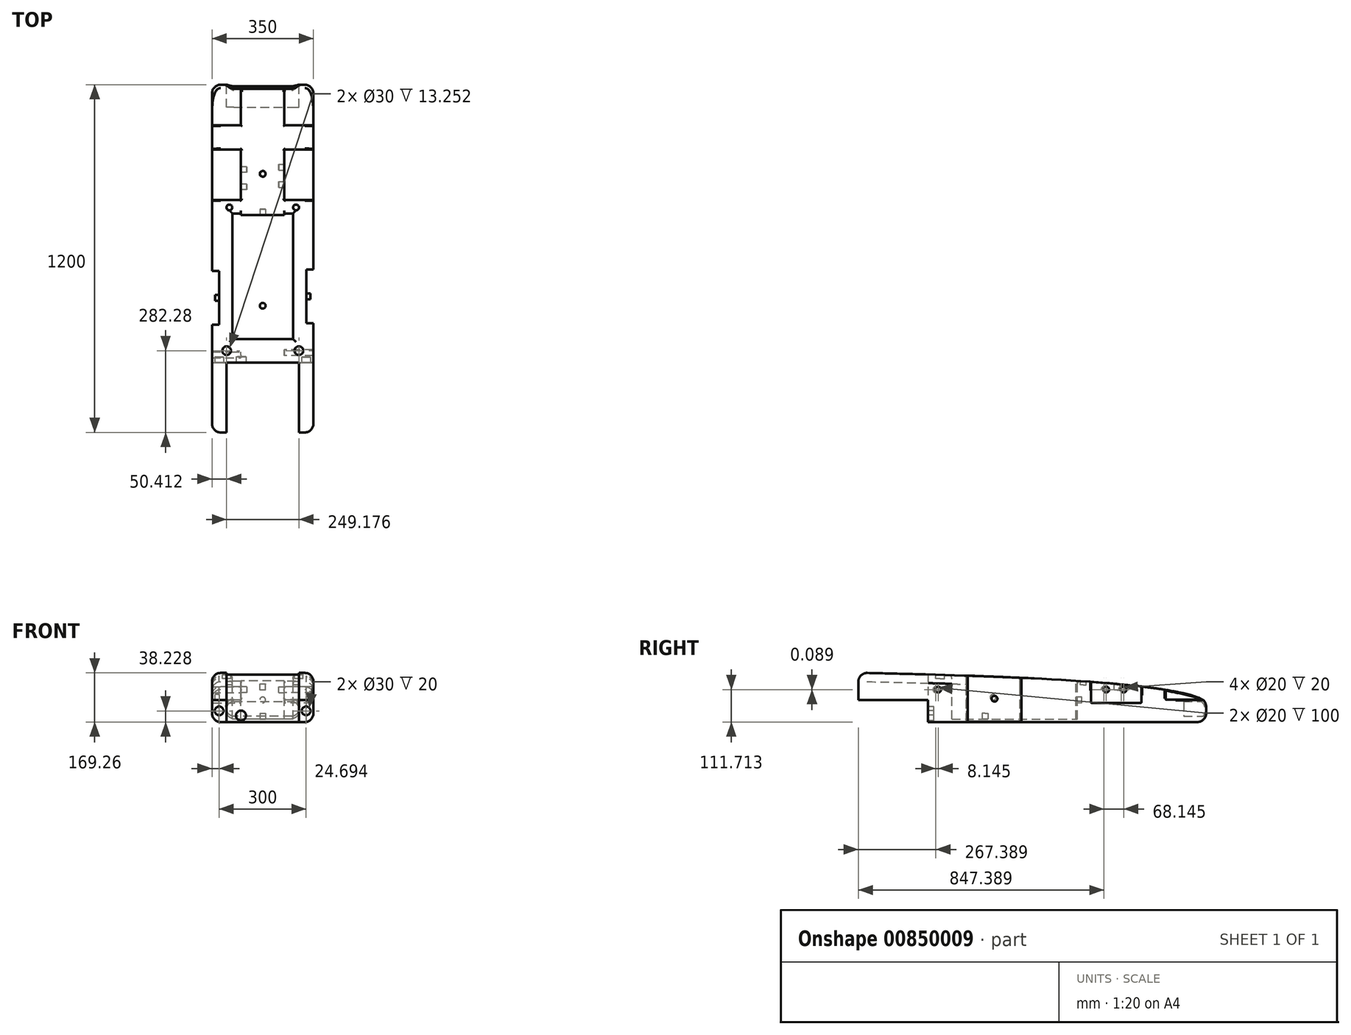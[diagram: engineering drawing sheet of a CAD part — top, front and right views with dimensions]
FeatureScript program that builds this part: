
annotation { "Feature Type Name" : "Feature", "Feature Type Description" : "" }
export const myFeature = defineFeature(function(context is Context, id is Id, definition is map)
    precondition{}
    {
        {
            var Q0;
            Q0=qCreatedBy(makeId("Right.planeOp"),FACE);
            var sketch = newSketch(context, id + "F0", { "sketchPlane" : qUnion([Q0])});
            skLineSegment(sketch, "E0", {"start": v(-322.28, 0) * mm, "end": v(877.72, 0) * mm});
            skLineSegment(sketch, "E1", {"start": v(-322.28, 0) * mm, "end": v(-322.28, 170) * mm});
            skLineSegment(sketch, "E2", {"start": v(877.72, 0) * mm, "end": v(877.72, 70) * mm});
            skFitSpline(sketch, "E3", {"points": [v(877.72, 70) * mm, v(-322.28, 170) * mm], "startDerivative": vector(-305.27, 234.76) * mm, "endDerivative": vector(-966.84, 23.9) * mm});
            skSolve(sketch);
        }
        {
            var Q0;
            Q0=makeQuery(id+"F0.imprint","IMPRINT",FACE,{"disambiguationData":[TD([[makeQuery(id+"F0.imprint","IMPRINT",EDGE,{"derivedFrom":sQuery(id+"F0.wireOp",EDGE,"E0")}),1.0]])]});
            extrude(context, id + "F1", {"entities" : qUnion([Q0]), "endBound" : BoundingType.SYMMETRIC, "depth" : 350 * mm, "offsetDistance" : 25 * mm});
        }
        {
            var Q0;
            Q0=makeQuery(id+"F1.opExtrude","SWEPT_EDGE",EDGE,{"disambiguationData":[OSD([sQuery(id+"F0.wireOp",EDGE,"E2"),sQuery(id+"F0.wireOp",EDGE,"E3")])]});
            var Q1;
            Q1=makeQuery(id+"F1.opExtrude","CAP_EDGE",EDGE,{"disambiguationData":[OSD([sQuery(id+"F0.wireOp",EDGE,"E2")])],"isStart":false});
            var Q2;
            Q2=makeQuery(id+"F1.opExtrude","SWEPT_EDGE",EDGE,{"disambiguationData":[OSD([sQuery(id+"F0.wireOp",EDGE,"E0"),sQuery(id+"F0.wireOp",EDGE,"E2")])]});
            var Q3;
            Q3=makeQuery(id+"F1.opExtrude","CAP_EDGE",EDGE,{"disambiguationData":[OSD([sQuery(id+"F0.wireOp",EDGE,"E2")])],"isStart":true});
            var Q4;
            Q4=makeQuery(id+"F1.opExtrude","CAP_EDGE",EDGE,{"disambiguationData":[OSD([sQuery(id+"F0.wireOp",EDGE,"E0")])],"isStart":false});
            var Q5;
            Q5=makeQuery(id+"F1.opExtrude","CAP_EDGE",EDGE,{"disambiguationData":[OSD([sQuery(id+"F0.wireOp",EDGE,"E3")])],"isStart":false});
            var Q6;
            Q6=makeQuery(id+"F1.opExtrude","CAP_EDGE",EDGE,{"disambiguationData":[OSD([sQuery(id+"F0.wireOp",EDGE,"E1")])],"isStart":false});
            var Q7;
            Q7=makeQuery(id+"F1.opExtrude","CAP_EDGE",EDGE,{"disambiguationData":[OSD([sQuery(id+"F0.wireOp",EDGE,"E0")])],"isStart":true});
            var Q8;
            Q8=makeQuery(id+"F1.opExtrude","CAP_EDGE",EDGE,{"disambiguationData":[OSD([sQuery(id+"F0.wireOp",EDGE,"E3")])],"isStart":true});
            var Q9;
            Q9=makeQuery(id+"F1.opExtrude","CAP_EDGE",EDGE,{"disambiguationData":[OSD([sQuery(id+"F0.wireOp",EDGE,"E1")])],"isStart":true});
            var Q10;
            Q10=makeQuery(id+"F1.opExtrude","SWEPT_EDGE",EDGE,{"disambiguationData":[OSD([sQuery(id+"F0.wireOp",EDGE,"E1"),sQuery(id+"F0.wireOp",EDGE,"E3")])]});
            var Q11;
            Q11=makeQuery(id+"F1.opExtrude","SWEPT_EDGE",EDGE,{"disambiguationData":[OSD([sQuery(id+"F0.wireOp",EDGE,"E0"),sQuery(id+"F0.wireOp",EDGE,"E1")])]});
            fillet(context, id + "F2", {"entities" : qUnion([Q0, Q1, Q2, Q3, Q4, Q5, Q6, Q7, Q8, Q9, Q10, Q11]), "radius" : 30 * mm, "tangentPropagation" : true, "allowEdgeOverflow" : false});
        }
        {
            var Q0;
            Q0=qCreatedBy(makeId("Front.planeOp"),FACE);
            cPlane(context, id + "F3", {"entities" : qUnion([Q0]), "cplaneType" : CPlaneType.OFFSET, "offset" : 1500 * mm, "oppositeDirection" : true, "width" : 150 * mm, "height" : 150 * mm});
        }
        {
            var Q0;
            Q0=qCreatedBy(id+"F3.planeOp",FACE);
            var sketch = newSketch(context, id + "F4", { "sketchPlane" : qUnion([Q0])});
            skLineSegment(sketch, "E4.bottom", {"start": v(-100, 20.2) * mm, "end": v(100, 20.2) * mm});
            skLineSegment(sketch, "E4.top", {"start": v(-100, 70.2) * mm, "end": v(100, 70.2) * mm});
            skLineSegment(sketch, "E4.left", {"start": v(-100, 20.2) * mm, "end": v(-100, 70.2) * mm});
            skLineSegment(sketch, "E4.right", {"start": v(100, 20.2) * mm, "end": v(100, 70.2) * mm});
            skPoint(sketch, "E4.middle", {"position": v(0, 45.2) * mm});
            skArc(sketch, "E5", {"start": v(-100, 70.2) * mm, "mid": v(-125, 45.2) * mm, "end": v(-100, 20.2) * mm});
            skArc(sketch, "E6", {"start": v(100, 20.2) * mm, "mid": v(125, 45.2) * mm, "end": v(100, 70.2) * mm});
            skSolve(sketch);
        }
        {
            var Q0;
            Q0=makeQuery(id+"F4.imprint","IMPRINT",FACE,{"disambiguationData":[TD([[makeQuery(id+"F4.imprint","IMPRINT",EDGE,{"derivedFrom":sQuery(id+"F4.wireOp",EDGE,"E4.bottom")}),1.0]])]});
            var Q1;
            Q1=makeQuery(id+"F4.imprint","IMPRINT",FACE,{"disambiguationData":[TD([[makeQuery(id+"F4.imprint","IMPRINT",EDGE,{"derivedFrom":sQuery(id+"F4.wireOp",EDGE,"E4.left")}),1.0]])]});
            var Q2;
            Q2=makeQuery(id+"F4.imprint","IMPRINT",FACE,{"disambiguationData":[TD([[makeQuery(id+"F4.imprint","IMPRINT",EDGE,{"derivedFrom":sQuery(id+"F4.wireOp",EDGE,"E4.right")}),-1.0]])]});
            extrude(context, id + "F5", {"entities" : qUnion([Q0, Q1, Q2]), "operationType" : NewBodyOperationType.REMOVE, "depth" : 700 * mm, "offsetDistance" : 25 * mm});
        }
        {
            var Q0;
            {var subQ0=sQuery(id+"F0.wireOp",EDGE,"E3");var subQ1=sQuery(id+"F0.wireOp",EDGE,"E2");Q0=makeQuery(id+"F5.boolean.opBoolean","INTERSECT",EDGE,{"derivedFrom":[makeQuery(id+"F2.opFillet","BLEND_FACE",FACE,{"disambiguationData":[OSD([subQ1,subQ0]),TDD([makeQuery(id+"F1.opExtrude","SWEPT_EDGE",EDGE,{"disambiguationData":[OSD([subQ1,subQ0])]})])]}),makeQuery(id+"F5.opExtrude","SWEPT_FACE",FACE,{"disambiguationData":[OSD([sQuery(id+"F4.wireOp",EDGE,"E4.top")])]})]});}
            var Q1;
            {var subQ0=sQuery(id+"F0.wireOp",EDGE,"E2");var subQ1=sQuery(id+"F0.wireOp",EDGE,"E0");Q1=makeQuery(id+"F5.boolean.opBoolean","INTERSECT",EDGE,{"derivedFrom":[makeQuery(id+"F2.opFillet","BLEND_FACE",FACE,{"disambiguationData":[OSD([subQ1,subQ0]),TDD([makeQuery(id+"F1.opExtrude","SWEPT_EDGE",EDGE,{"disambiguationData":[OSD([subQ1,subQ0])]})])]}),makeQuery(id+"F5.opExtrude","SWEPT_FACE",FACE,{"disambiguationData":[OSD([sQuery(id+"F4.wireOp",EDGE,"E4.bottom")])]})]});}
            var Q2;
            Q2=makeQuery(id+"F5.boolean.opBoolean","INTERSECT",EDGE,{"derivedFrom":[makeQuery(id+"F1.opExtrude","SWEPT_FACE",FACE,{"disambiguationData":[OSD([sQuery(id+"F0.wireOp",EDGE,"E2")])]}),makeQuery(id+"F5.opExtrude","SWEPT_FACE",FACE,{"disambiguationData":[OSD([sQuery(id+"F4.wireOp",EDGE,"E4.right")])]})]});
            var Q3;
            {var subQ0=sQuery(id+"F0.wireOp",EDGE,"E2");var subQ1=sQuery(id+"F0.wireOp",EDGE,"E0");Q3=makeQuery(id+"F5.boolean.opBoolean","INTERSECT",EDGE,{"derivedFrom":[makeQuery(id+"F2.opFillet","BLEND_FACE",FACE,{"disambiguationData":[OSD([subQ1,subQ0]),TDD([makeQuery(id+"F1.opExtrude","SWEPT_EDGE",EDGE,{"disambiguationData":[OSD([subQ1,subQ0])]})])]}),makeQuery(id+"F5.opExtrude","SWEPT_FACE",FACE,{"disambiguationData":[OSD([sQuery(id+"F4.wireOp",EDGE,"E4.right")])]})]});}
            var Q4;
            {var subQ0=sQuery(id+"F0.wireOp",EDGE,"E3");var subQ1=sQuery(id+"F0.wireOp",EDGE,"E2");Q4=makeQuery(id+"F5.boolean.opBoolean","INTERSECT",EDGE,{"derivedFrom":[makeQuery(id+"F2.opFillet","BLEND_FACE",FACE,{"disambiguationData":[OSD([subQ1,subQ0]),TDD([makeQuery(id+"F1.opExtrude","SWEPT_EDGE",EDGE,{"disambiguationData":[OSD([subQ1,subQ0])]})])]}),makeQuery(id+"F5.opExtrude","SWEPT_FACE",FACE,{"disambiguationData":[OSD([sQuery(id+"F4.wireOp",EDGE,"E4.right")])]})]});}
            var Q5;
            {var subQ0=sQuery(id+"F0.wireOp",EDGE,"E3");var subQ1=sQuery(id+"F0.wireOp",EDGE,"E2");Q5=makeQuery(id+"F5.boolean.opBoolean","INTERSECT",EDGE,{"derivedFrom":[makeQuery(id+"F2.opFillet","BLEND_FACE",FACE,{"disambiguationData":[OSD([subQ1,subQ0]),TDD([makeQuery(id+"F1.opExtrude","SWEPT_EDGE",EDGE,{"disambiguationData":[OSD([subQ1,subQ0])]})])]}),makeQuery(id+"F5.opExtrude","SWEPT_FACE",FACE,{"disambiguationData":[OSD([sQuery(id+"F4.wireOp",EDGE,"E4.left")])]})]});}
            var Q6;
            Q6=makeQuery(id+"F5.boolean.opBoolean","INTERSECT",EDGE,{"derivedFrom":[makeQuery(id+"F1.opExtrude","SWEPT_FACE",FACE,{"disambiguationData":[OSD([sQuery(id+"F0.wireOp",EDGE,"E2")])]}),makeQuery(id+"F5.opExtrude","SWEPT_FACE",FACE,{"disambiguationData":[OSD([sQuery(id+"F4.wireOp",EDGE,"E4.left")])]})]});
            var Q7;
            {var subQ0=sQuery(id+"F0.wireOp",EDGE,"E2");var subQ1=sQuery(id+"F0.wireOp",EDGE,"E0");Q7=makeQuery(id+"F5.boolean.opBoolean","INTERSECT",EDGE,{"derivedFrom":[makeQuery(id+"F2.opFillet","BLEND_FACE",FACE,{"disambiguationData":[OSD([subQ1,subQ0]),TDD([makeQuery(id+"F1.opExtrude","SWEPT_EDGE",EDGE,{"disambiguationData":[OSD([subQ1,subQ0])]})])]}),makeQuery(id+"F5.opExtrude","SWEPT_FACE",FACE,{"disambiguationData":[OSD([sQuery(id+"F4.wireOp",EDGE,"E4.left")])]})]});}
            fillet(context, id + "F6", {"entities" : qUnion([Q0, Q1, Q2, Q3, Q4, Q5, Q6, Q7]), "radius" : 5 * mm, "tangentPropagation" : true, "allowEdgeOverflow" : false});
        }
        {
            var Q0;
            Q0=makeQuery(id+"F1.opExtrude","SWEPT_FACE",FACE,{"disambiguationData":[OSD([sQuery(id+"F0.wireOp",EDGE,"E0")])]});
            cPlane(context, id + "F7", {"entities" : qUnion([Q0]), "cplaneType" : CPlaneType.OFFSET, "offset" : 480 * mm, "oppositeDirection" : true, "width" : 150 * mm, "height" : 150 * mm});
        }
        {
            var Q0;
            Q0=qCreatedBy(id+"F7.planeOp",FACE);
            var sketch = newSketch(context, id + "F8", { "sketchPlane" : qUnion([Q0])});
            skLineSegment(sketch, "E7.bottom", {"start": v(197.8, -871.85) * mm, "end": v(75, -871.85) * mm});
            skLineSegment(sketch, "E7.top", {"start": v(197.8, -737.79) * mm, "end": v(75, -737.79) * mm});
            skLineSegment(sketch, "E7.left", {"start": v(197.8, -871.85) * mm, "end": v(197.8, -737.79) * mm});
            skLineSegment(sketch, "E7.right", {"start": v(75, -871.85) * mm, "end": v(75, -737.79) * mm});
            skLineSegment(sketch, "E8", {"start": v(0, -789.69) * mm, "end": v(0, -1590.06) * mm});
            skLineSegment(sketch, "E9.MirrorCS", {"start": v(-75, -871.85) * mm, "end": v(-75, -737.79) * mm});
            skLineSegment(sketch, "E10.MirrorCS", {"start": v(-197.8, -737.79) * mm, "end": v(-75, -737.79) * mm});
            skLineSegment(sketch, "E11.MirrorCS", {"start": v(-197.8, -871.85) * mm, "end": v(-197.8, -737.79) * mm});
            skLineSegment(sketch, "E12.MirrorCS", {"start": v(-197.8, -871.85) * mm, "end": v(-75, -871.85) * mm});
            skLineSegment(sketch, "E13.bottom", {"start": v(197.8, -480.68) * mm, "end": v(75, -480.68) * mm});
            skLineSegment(sketch, "E13.top", {"start": v(197.8, -654.04) * mm, "end": v(75, -654.04) * mm});
            skLineSegment(sketch, "E13.left", {"start": v(197.8, -654.04) * mm, "end": v(197.8, -480.68) * mm});
            skLineSegment(sketch, "E13.right", {"start": v(75, -654.04) * mm, "end": v(75, -480.68) * mm});
            skLineSegment(sketch, "E14.MirrorCS", {"start": v(-197.8, -654.04) * mm, "end": v(-75, -654.04) * mm});
            skLineSegment(sketch, "E15.MirrorCS", {"start": v(-75, -654.04) * mm, "end": v(-75, -480.68) * mm});
            skLineSegment(sketch, "E16.MirrorCS", {"start": v(-197.8, -480.68) * mm, "end": v(-75, -480.68) * mm});
            skLineSegment(sketch, "E17.MirrorCS", {"start": v(-197.8, -654.04) * mm, "end": v(-197.8, -480.68) * mm});
            skLineSegment(sketch, "E18.bottom", {"start": v(104.59, 0) * mm, "end": v(-104.59, 0) * mm});
            skLineSegment(sketch, "E18.top", {"start": v(104.59, -433.3) * mm, "end": v(-104.59, -433.3) * mm});
            skLineSegment(sketch, "E18.left", {"start": v(104.59, 0) * mm, "end": v(104.59, -433.3) * mm});
            skLineSegment(sketch, "E18.right", {"start": v(-104.59, 0) * mm, "end": v(-104.59, -433.3) * mm});
            skPoint(sketch, "E18.middle", {"position": v(0, -216.65) * mm});
            skLineSegment(sketch, "E19.bottom", {"start": v(75, -448.3) * mm, "end": v(-75, -448.3) * mm});
            skLineSegment(sketch, "E19.top", {"start": v(75, -428.3) * mm, "end": v(-75, -428.3) * mm});
            skLineSegment(sketch, "E19.left", {"start": v(75, -448.3) * mm, "end": v(75, -428.3) * mm});
            skLineSegment(sketch, "E19.right", {"start": v(-75, -448.3) * mm, "end": v(-75, -428.3) * mm});
            skPoint(sketch, "E19.middle", {"position": v(0, -438.3) * mm});
            skCircle(sketch, "E20", {"center": v(0, -570.33) * mm, "radius": 10 * mm});
            skCircle(sketch, "E21", {"center": v(115, -454.3) * mm, "radius": 10 * mm});
            skCircle(sketch, "E22", {"center": v(-115, -454.3) * mm, "radius": 10 * mm});
            skCircle(sketch, "E23", {"center": v(-124.59, 40) * mm, "radius": 15 * mm});
            skCircle(sketch, "E24", {"center": v(124.59, 40) * mm, "radius": 15 * mm});
            skSolve(sketch);
        }
        {
            var Q0;
            Q0=makeQuery(id+"F8.imprint","IMPRINT",FACE,{"disambiguationData":[TD([[makeQuery(id+"F8.imprint","IMPRINT",EDGE,{"derivedFrom":sQuery(id+"F8.wireOp",EDGE,"E7.bottom")}),-1.0]])]});
            var Q1;
            Q1=makeQuery(id+"F8.imprint","IMPRINT",FACE,{"disambiguationData":[TD([[makeQuery(id+"F8.imprint","IMPRINT",EDGE,{"derivedFrom":sQuery(id+"F8.wireOp",EDGE,"E9.MirrorCS")}),1.0]])]});
            extrude(context, id + "F9", {"entities" : qUnion([Q0, Q1]), "operationType" : NewBodyOperationType.REMOVE, "depth" : 403 * mm, "offsetDistance" : 25 * mm});
        }
        {
            var Q0;
            Q0=makeQuery(id+"F8.imprint","IMPRINT",FACE,{"disambiguationData":[TD([[makeQuery(id+"F8.imprint","IMPRINT",EDGE,{"derivedFrom":sQuery(id+"F8.wireOp",EDGE,"E13.bottom")}),1.0]])]});
            var Q1;
            Q1=makeQuery(id+"F8.imprint","IMPRINT",FACE,{"disambiguationData":[TD([[makeQuery(id+"F8.imprint","IMPRINT",EDGE,{"derivedFrom":sQuery(id+"F8.wireOp",EDGE,"E14.MirrorCS")}),1.0]])]});
            extrude(context, id + "F10", {"entities" : qUnion([Q0, Q1]), "operationType" : NewBodyOperationType.REMOVE, "depth" : 400 * mm, "offsetDistance" : 25 * mm});
        }
        {
            var Q0;
            Q0=makeQuery(id+"F8.imprint","IMPRINT",FACE,{"disambiguationData":[TD([[makeQuery(id+"F8.imprint","IMPRINT",EDGE,{"derivedFrom":sQuery(id+"F8.wireOp",EDGE,"E13.bottom")}),1.0]])]});
            var Q1;
            Q1=makeQuery(id+"F8.imprint","IMPRINT",FACE,{"disambiguationData":[TD([[makeQuery(id+"F8.imprint","IMPRINT",EDGE,{"derivedFrom":sQuery(id+"F8.wireOp",EDGE,"E14.MirrorCS")}),1.0]])]});
            extrude(context, id + "F11", {"entities" : qUnion([Q0, Q1]), "operationType" : NewBodyOperationType.REMOVE, "depth" : 415 * mm, "offsetDistance" : 25 * mm});
        }
        {
            var Q0;
            Q0=makeQuery(id+"F8.imprint","IMPRINT",FACE,{"disambiguationData":[TD([[makeQuery(id+"F8.imprint","IMPRINT",EDGE,{"derivedFrom":sQuery(id+"F8.wireOp",EDGE,"E18.bottom")}),1.0]])]});
            extrude(context, id + "F12", {"entities" : qUnion([Q0]), "operationType" : NewBodyOperationType.REMOVE, "depth" : 470 * mm, "offsetDistance" : 25 * mm});
        }
        {
            var Q0;
            Q0=makeQuery(id+"F12.boolean.opBoolean","INTERSECT",EDGE,{"derivedFrom":[makeQuery(id+"F1.opExtrude","SWEPT_FACE",FACE,{"disambiguationData":[OSD([sQuery(id+"F0.wireOp",EDGE,"E3")])]}),makeQuery(id+"F12.opExtrude","SWEPT_FACE",FACE,{"disambiguationData":[OSD([sQuery(id+"F8.wireOp",EDGE,"E18.bottom")])]})]});
            var Q1;
            Q1=makeQuery(id+"F12.boolean.opBoolean","INTERSECT",EDGE,{"derivedFrom":[makeQuery(id+"F1.opExtrude","SWEPT_FACE",FACE,{"disambiguationData":[OSD([sQuery(id+"F0.wireOp",EDGE,"E3")])]}),makeQuery(id+"F12.opExtrude","SWEPT_FACE",FACE,{"disambiguationData":[OSD([sQuery(id+"F8.wireOp",EDGE,"E18.right")])]})]});
            var Q2;
            Q2=makeQuery(id+"F12.boolean.opBoolean","INTERSECT",EDGE,{"derivedFrom":[makeQuery(id+"F1.opExtrude","SWEPT_FACE",FACE,{"disambiguationData":[OSD([sQuery(id+"F0.wireOp",EDGE,"E3")])]}),makeQuery(id+"F12.opExtrude","SWEPT_FACE",FACE,{"disambiguationData":[OSD([sQuery(id+"F8.wireOp",EDGE,"E18.left")])]})]});
            var Q3;
            Q3=makeQuery(id+"F12.boolean.opBoolean","INTERSECT",EDGE,{"derivedFrom":[makeQuery(id+"F1.opExtrude","SWEPT_FACE",FACE,{"disambiguationData":[OSD([sQuery(id+"F0.wireOp",EDGE,"E3")])]}),makeQuery(id+"F12.opExtrude","SWEPT_FACE",FACE,{"disambiguationData":[OSD([sQuery(id+"F8.wireOp",EDGE,"E18.top")])]})]});
            fillet(context, id + "F13", {"entities" : qUnion([Q0, Q1, Q2, Q3]), "radius" : 10 * mm, "tangentPropagation" : true, "allowEdgeOverflow" : false});
        }
        {
            var Q0;
            {var subQ3=sQuery(id+"F8.wireOp",EDGE,"E13.bottom");var subQ4=makeQuery(id+"F10.opExtrude","SWEPT_FACE",FACE,{"disambiguationData":[OSD([subQ3])]});var subQ5=sQuery(id+"F0.wireOp",EDGE,"E3");var subQ6=sQuery(id+"F0.wireOp",EDGE,"E2");var subQ7=sQuery(id+"F0.wireOp",EDGE,"E1");var subQ8=sQuery(id+"F0.wireOp",EDGE,"E0");var subQ9=makeQuery(id+"F1.opExtrude","CAP_FACE",FACE,{"disambiguationData":[OSD([subQ8,subQ7,subQ6,subQ5])],"isStart":false});Q0=makeQuery(id+"F11.boolean.opBoolean","SPLIT",FACE,{"disambiguationData":[TD([makeQuery(id+"F10.boolean.opBoolean","COPY",FACE,{"derivedFrom":subQ4})])],"derivedFrom":subQ9});}
            cPlane(context, id + "F14", {"entities" : qUnion([Q0]), "cplaneType" : CPlaneType.OFFSET, "offset" : 60 * mm, "width" : 150 * mm, "height" : 150 * mm});
        }
        {
            var Q0;
            {var subQ1=sQuery(id+"F8.wireOp",EDGE,"E16.MirrorCS");var subQ4=makeQuery(id+"F10.opExtrude","SWEPT_FACE",FACE,{"disambiguationData":[OSD([subQ1])]});var subQ5=sQuery(id+"F0.wireOp",EDGE,"E3");var subQ7=sQuery(id+"F0.wireOp",EDGE,"E2");var subQ8=sQuery(id+"F0.wireOp",EDGE,"E1");var subQ9=sQuery(id+"F0.wireOp",EDGE,"E0");var subQ10=makeQuery(id+"F1.opExtrude","CAP_FACE",FACE,{"disambiguationData":[OSD([subQ9,subQ8,subQ7,subQ5])],"isStart":true});Q0=makeQuery(id+"F11.boolean.opBoolean","SPLIT",FACE,{"disambiguationData":[TD([makeQuery(id+"F10.boolean.opBoolean","COPY",FACE,{"derivedFrom":subQ4})])],"derivedFrom":subQ10});}
            cPlane(context, id + "F15", {"entities" : qUnion([Q0]), "cplaneType" : CPlaneType.OFFSET, "offset" : 60 * mm, "width" : 150 * mm, "height" : 150 * mm});
        }
        {
            var Q0;
            Q0=qCreatedBy(id+"F14.planeOp",FACE);
            var sketch = newSketch(context, id + "F16", { "sketchPlane" : qUnion([Q0])});
            skLineSegment(sketch, "E25.bottom", {"start": v(240.12, -6.88) * mm, "end": v(55.12, -6.88) * mm});
            skLineSegment(sketch, "E25.top", {"start": v(240.12, 167.12) * mm, "end": v(55.12, 167.12) * mm});
            skLineSegment(sketch, "E25.left", {"start": v(240.12, -6.88) * mm, "end": v(240.12, 167.12) * mm});
            skLineSegment(sketch, "E25.right", {"start": v(55.12, -6.88) * mm, "end": v(55.12, 167.12) * mm});
            skPoint(sketch, "E25.middle", {"position": v(147.62, 80.12) * mm});
            skCircle(sketch, "E26", {"center": v(147.62, 80.12) * mm, "radius": 10 * mm});
            skSolve(sketch);
        }
        {
            var Q0;
            Q0=makeQuery(id+"F16.imprint","IMPRINT",FACE,{"disambiguationData":[TD([[makeQuery(id+"F16.imprint","IMPRINT",EDGE,{"derivedFrom":sQuery(id+"F16.wireOp",EDGE,"E25.bottom")}),-1.0]])]});
            extrude(context, id + "F17", {"entities" : qUnion([Q0]), "operationType" : NewBodyOperationType.REMOVE, "oppositeDirection" : true, "depth" : 85 * mm, "offsetDistance" : 25 * mm});
        }
        {
            var Q0;
            Q0=qCreatedBy(id+"F15.planeOp",FACE);
            var sketch = newSketch(context, id + "F18", { "sketchPlane" : qUnion([Q0])});
            skLineSegment(sketch, "E27.bottom", {"start": v(-50.04, -1.77) * mm, "end": v(-235.04, -1.77) * mm});
            skLineSegment(sketch, "E27.top", {"start": v(-50.04, 172.23) * mm, "end": v(-235.04, 172.23) * mm});
            skLineSegment(sketch, "E27.left", {"start": v(-50.04, -1.77) * mm, "end": v(-50.04, 172.23) * mm});
            skLineSegment(sketch, "E27.right", {"start": v(-235.04, -1.77) * mm, "end": v(-235.04, 172.23) * mm});
            skPoint(sketch, "E27.middle", {"position": v(-142.54, 85.23) * mm});
            skCircle(sketch, "E28", {"center": v(-142.54, 85.23) * mm, "radius": 10 * mm});
            skSolve(sketch);
        }
        {
            var Q0;
            Q0=makeQuery(id+"F18.imprint","IMPRINT",FACE,{"disambiguationData":[TD([[makeQuery(id+"F18.imprint","IMPRINT",EDGE,{"derivedFrom":sQuery(id+"F18.wireOp",EDGE,"E27.bottom")}),-1.0]])]});
            extrude(context, id + "F19", {"entities" : qUnion([Q0]), "operationType" : NewBodyOperationType.REMOVE, "oppositeDirection" : true, "depth" : 85 * mm, "offsetDistance" : 25 * mm});
        }
        {
            var Q0;
            Q0=makeQuery(id+"F8.imprint","IMPRINT",FACE,{"disambiguationData":[TD([[makeQuery(id+"F8.imprint","IMPRINT",EDGE,{"derivedFrom":sQuery(id+"F8.wireOp",EDGE,"E20")}),1.0]])]});
            extrude(context, id + "F20", {"entities" : qUnion([Q0]), "operationType" : NewBodyOperationType.REMOVE, "depth" : 370 * mm, "offsetDistance" : 25 * mm});
        }
        {
            var Q0;
            Q0=makeQuery(id+"F17.boolean.opBoolean","SPLIT",FACE,{"disambiguationData":[TD([makeQuery(id+"F17.opExtrude","SWEPT_FACE",FACE,{"disambiguationData":[OSD([sQuery(id+"F16.wireOp",EDGE,"E26")])]})])],"derivedFrom":makeQuery(id+"F1.opExtrude","CAP_FACE",FACE,{"disambiguationData":[OSD([sQuery(id+"F0.wireOp",EDGE,"E0"),sQuery(id+"F0.wireOp",EDGE,"E1"),sQuery(id+"F0.wireOp",EDGE,"E2"),sQuery(id+"F0.wireOp",EDGE,"E3")])],"isStart":false})});
            extrude(context, id + "F21", {"entities" : qUnion([Q0]), "operationType" : NewBodyOperationType.REMOVE, "oppositeDirection" : true, "depth" : 10 * mm, "offsetDistance" : 25 * mm});
        }
        {
            var Q0;
            Q0=makeQuery(id+"F19.boolean.opBoolean","SPLIT",FACE,{"disambiguationData":[TD([makeQuery(id+"F19.opExtrude","SWEPT_FACE",FACE,{"disambiguationData":[OSD([sQuery(id+"F18.wireOp",EDGE,"E28")])]})])],"derivedFrom":makeQuery(id+"F1.opExtrude","CAP_FACE",FACE,{"disambiguationData":[OSD([sQuery(id+"F0.wireOp",EDGE,"E0"),sQuery(id+"F0.wireOp",EDGE,"E1"),sQuery(id+"F0.wireOp",EDGE,"E2"),sQuery(id+"F0.wireOp",EDGE,"E3")])],"isStart":true})});
            extrude(context, id + "F22", {"entities" : qUnion([Q0]), "operationType" : NewBodyOperationType.REMOVE, "oppositeDirection" : true, "depth" : 10 * mm, "offsetDistance" : 25 * mm});
        }
        {
            var Q0;
            Q0=makeQuery(id+"F1.opExtrude","SWEPT_FACE",FACE,{"disambiguationData":[OSD([sQuery(id+"F0.wireOp",EDGE,"E1")])]});
            cPlane(context, id + "F23", {"entities" : qUnion([Q0]), "cplaneType" : CPlaneType.OFFSET, "offset" : 109 * mm, "width" : 150 * mm, "height" : 150 * mm});
        }
        {
            var Q0;
            Q0=qCreatedBy(id+"F23.planeOp",FACE);
            var sketch = newSketch(context, id + "F24", { "sketchPlane" : qUnion([Q0])});
            skLineSegment(sketch, "E29.bottom", {"start": v(125, -217.5) * mm, "end": v(-125, -217.5) * mm});
            skLineSegment(sketch, "E29.top", {"start": v(125, 217.5) * mm, "end": v(-125, 217.5) * mm});
            skLineSegment(sketch, "E29.left", {"start": v(125, -217.5) * mm, "end": v(125, 217.5) * mm});
            skLineSegment(sketch, "E29.right", {"start": v(-125, -217.5) * mm, "end": v(-125, 217.5) * mm});
            skPoint(sketch, "E29.middle", {"position": v(0, 0) * mm});
            skSolve(sketch);
        }
        {
            var Q0;
            Q0=makeQuery(id+"F24.imprint","IMPRINT",FACE,{"disambiguationData":[TD([[makeQuery(id+"F24.imprint","IMPRINT",EDGE,{"derivedFrom":sQuery(id+"F24.wireOp",EDGE,"E29.bottom")}),-1.0]])]});
            extrude(context, id + "F25", {"entities" : qUnion([Q0]), "operationType" : NewBodyOperationType.REMOVE, "oppositeDirection" : true, "depth" : 350 * mm, "offsetDistance" : 25 * mm});
        }
        {
            var Q0;
            Q0=makeQuery(id+"F1.opExtrude","SWEPT_FACE",FACE,{"disambiguationData":[OSD([sQuery(id+"F0.wireOp",EDGE,"E0")])]});
            cPlane(context, id + "F26", {"entities" : qUnion([Q0]), "cplaneType" : CPlaneType.OFFSET, "offset" : 117 * mm, "width" : 150 * mm, "height" : 150 * mm});
        }
        {
            var Q0;
            Q0=qCreatedBy(id+"F26.planeOp",FACE);
            var sketch = newSketch(context, id + "F27", { "sketchPlane" : qUnion([Q0])});
            skLineSegment(sketch, "E30.bottom", {"start": v(227.84, 81.71) * mm, "end": v(-227.84, 81.71) * mm});
            skLineSegment(sketch, "E30.top", {"start": v(227.84, 498.02) * mm, "end": v(-227.84, 498.02) * mm});
            skLineSegment(sketch, "E30.left", {"start": v(227.84, 81.71) * mm, "end": v(227.84, 498.02) * mm});
            skLineSegment(sketch, "E30.right", {"start": v(-227.84, 81.71) * mm, "end": v(-227.84, 498.02) * mm});
            skPoint(sketch, "E30.middle", {"position": v(0, 289.87) * mm});
            skSolve(sketch);
        }
        {
            var Q0;
            Q0=makeQuery(id+"F27.imprint","IMPRINT",FACE,{"disambiguationData":[TD([[makeQuery(id+"F27.imprint","IMPRINT",EDGE,{"derivedFrom":sQuery(id+"F27.wireOp",EDGE,"E30.bottom")}),-1.0]])]});
            extrude(context, id + "F28", {"entities" : qUnion([Q0]), "operationType" : NewBodyOperationType.REMOVE, "oppositeDirection" : true, "depth" : 193 * mm, "offsetDistance" : 25 * mm});
        }
        {
            var Q0;
            Q0=makeQuery(id+"F12.boolean.opBoolean","COPY",FACE,{"derivedFrom":makeQuery(id+"F12.opExtrude","CAP_FACE",FACE,{"disambiguationData":[OSD([sQuery(id+"F8.wireOp",EDGE,"E18.bottom"),sQuery(id+"F8.wireOp",EDGE,"E18.top"),sQuery(id+"F8.wireOp",EDGE,"E18.left"),sQuery(id+"F8.wireOp",EDGE,"E18.right"),sQuery(id+"F8.wireOp",EDGE,"E19.top"),sQuery(id+"F8.wireOp",EDGE,"E19.left"),sQuery(id+"F8.wireOp",EDGE,"E19.right")])],"isStart":false})});
            var sketch = newSketch(context, id + "F29", { "sketchPlane" : qUnion([Q0])});
            skLineSegment(sketch, "E31.bottom", {"start": v(104.59, 0) * mm, "end": v(-104.59, 0) * mm});
            skLineSegment(sketch, "E31.top", {"start": v(104.59, 230) * mm, "end": v(-104.59, 230) * mm});
            skLineSegment(sketch, "E31.left", {"start": v(104.59, 0) * mm, "end": v(104.59, 230) * mm});
            skLineSegment(sketch, "E31.right", {"start": v(-104.59, 0) * mm, "end": v(-104.59, 230) * mm});
            skCircle(sketch, "E32", {"center": v(0, 115) * mm, "radius": 10 * mm});
            skPoint(sketch, "E32.centerSnap0", {"position": v(104.59, 115) * mm});
            skSolve(sketch);
        }
        {
            var Q0;
            Q0=makeQuery(id+"F29.imprint","IMPRINT",FACE,{"disambiguationData":[TD([[makeQuery(id+"F29.imprint","IMPRINT",EDGE,{"derivedFrom":sQuery(id+"F29.wireOp",EDGE,"E32")}),1.0]])]});
            extrude(context, id + "F30", {"entities" : qUnion([Q0]), "operationType" : NewBodyOperationType.ADD, "depth" : 20 * mm, "offsetDistance" : 25 * mm});
        }
        {
            var Q0;
            Q0=makeQuery(id+"F9.boolean.opBoolean","INTERSECT",EDGE,{"derivedFrom":[makeQuery(id+"F1.opExtrude","SWEPT_FACE",FACE,{"disambiguationData":[OSD([sQuery(id+"F0.wireOp",EDGE,"E3")])]}),makeQuery(id+"F9.opExtrude","SWEPT_FACE",FACE,{"disambiguationData":[OSD([sQuery(id+"F8.wireOp",EDGE,"E7.right")])]})]});
            var Q1;
            Q1=makeQuery(id+"F9.boolean.opBoolean","INTERSECT",EDGE,{"derivedFrom":[makeQuery(id+"F1.opExtrude","SWEPT_FACE",FACE,{"disambiguationData":[OSD([sQuery(id+"F0.wireOp",EDGE,"E3")])]}),makeQuery(id+"F9.opExtrude","SWEPT_FACE",FACE,{"disambiguationData":[OSD([sQuery(id+"F8.wireOp",EDGE,"E9.MirrorCS")])]})]});
            var Q2;
            Q2=makeQuery(id+"F10.boolean.opBoolean","INTERSECT",EDGE,{"derivedFrom":[makeQuery(id+"F1.opExtrude","SWEPT_FACE",FACE,{"disambiguationData":[OSD([sQuery(id+"F0.wireOp",EDGE,"E3")])]}),makeQuery(id+"F10.opExtrude","SWEPT_FACE",FACE,{"disambiguationData":[OSD([sQuery(id+"F8.wireOp",EDGE,"E13.top")])]})]});
            var Q3;
            {var subQ0=sQuery(id+"F0.wireOp",EDGE,"E3");var subQ1=makeQuery(id+"F1.opExtrude","SWEPT_FACE",FACE,{"disambiguationData":[OSD([subQ0])]});var subQ2=makeQuery(id+"F1.opExtrude","CAP_EDGE",EDGE,{"disambiguationData":[OSD([subQ0])],"isStart":false});Q3=makeQuery(id+"F10.boolean.opBoolean","SPLIT",EDGE,{"disambiguationData":[TD([makeQuery(id+"F9.boolean.opBoolean","COPY",FACE,{"derivedFrom":makeQuery(id+"F9.opExtrude","SWEPT_FACE",FACE,{"disambiguationData":[OSD([sQuery(id+"F8.wireOp",EDGE,"E7.top")])]})})])],"derivedFrom":makeQuery(id+"F2.opFillet","BLEND_EDGE",EDGE,{"blendedFrom":[subQ2,subQ1],"blendedInto":[subQ1]})});}
            var Q4;
            Q4=makeQuery(id+"F9.boolean.opBoolean","INTERSECT",EDGE,{"derivedFrom":[makeQuery(id+"F1.opExtrude","SWEPT_FACE",FACE,{"disambiguationData":[OSD([sQuery(id+"F0.wireOp",EDGE,"E3")])]}),makeQuery(id+"F9.opExtrude","SWEPT_FACE",FACE,{"disambiguationData":[OSD([sQuery(id+"F8.wireOp",EDGE,"E7.top")])]})]});
            var Q5;
            Q5=makeQuery(id+"F9.boolean.opBoolean","INTERSECT",EDGE,{"derivedFrom":[makeQuery(id+"F1.opExtrude","SWEPT_FACE",FACE,{"disambiguationData":[OSD([sQuery(id+"F0.wireOp",EDGE,"E3")])]}),makeQuery(id+"F9.opExtrude","SWEPT_FACE",FACE,{"disambiguationData":[OSD([sQuery(id+"F8.wireOp",EDGE,"E10.MirrorCS")])]})]});
            var Q6;
            {var subQ0=sQuery(id+"F0.wireOp",EDGE,"E3");var subQ1=makeQuery(id+"F1.opExtrude","SWEPT_FACE",FACE,{"disambiguationData":[OSD([subQ0])]});var subQ2=makeQuery(id+"F1.opExtrude","CAP_EDGE",EDGE,{"disambiguationData":[OSD([subQ0])],"isStart":true});Q6=makeQuery(id+"F10.boolean.opBoolean","SPLIT",EDGE,{"disambiguationData":[TD([makeQuery(id+"F9.boolean.opBoolean","COPY",FACE,{"derivedFrom":makeQuery(id+"F9.opExtrude","SWEPT_FACE",FACE,{"disambiguationData":[OSD([sQuery(id+"F8.wireOp",EDGE,"E10.MirrorCS")])]})})])],"derivedFrom":makeQuery(id+"F2.opFillet","BLEND_EDGE",EDGE,{"blendedFrom":[subQ2,subQ1],"blendedInto":[subQ1]})});}
            var Q7;
            Q7=makeQuery(id+"F10.boolean.opBoolean","INTERSECT",EDGE,{"derivedFrom":[makeQuery(id+"F1.opExtrude","SWEPT_FACE",FACE,{"disambiguationData":[OSD([sQuery(id+"F0.wireOp",EDGE,"E3")])]}),makeQuery(id+"F10.opExtrude","SWEPT_FACE",FACE,{"disambiguationData":[OSD([sQuery(id+"F8.wireOp",EDGE,"E14.MirrorCS")])]})]});
            var Q8;
            Q8=makeQuery(id+"F10.boolean.opBoolean","INTERSECT",EDGE,{"derivedFrom":[makeQuery(id+"F1.opExtrude","SWEPT_FACE",FACE,{"disambiguationData":[OSD([sQuery(id+"F0.wireOp",EDGE,"E3")])]}),makeQuery(id+"F10.opExtrude","SWEPT_FACE",FACE,{"disambiguationData":[OSD([sQuery(id+"F8.wireOp",EDGE,"E15.MirrorCS")])]})]});
            var Q9;
            Q9=makeQuery(id+"F10.boolean.opBoolean","INTERSECT",EDGE,{"derivedFrom":[makeQuery(id+"F1.opExtrude","SWEPT_FACE",FACE,{"disambiguationData":[OSD([sQuery(id+"F0.wireOp",EDGE,"E3")])]}),makeQuery(id+"F10.opExtrude","SWEPT_FACE",FACE,{"disambiguationData":[OSD([sQuery(id+"F8.wireOp",EDGE,"E13.right")])]})]});
            var Q10;
            Q10=makeQuery(id+"F9.boolean.opBoolean","COPY",EDGE,{"derivedFrom":makeQuery(id+"F9.opExtrude","CAP_EDGE",EDGE,{"disambiguationData":[OSD([sQuery(id+"F8.wireOp",EDGE,"E7.top")])],"isStart":false})});
            var Q11;
            Q11=makeQuery(id+"F9.boolean.opBoolean","COPY",EDGE,{"derivedFrom":makeQuery(id+"F9.opExtrude","CAP_EDGE",EDGE,{"disambiguationData":[OSD([sQuery(id+"F8.wireOp",EDGE,"E7.right")])],"isStart":false})});
            var Q12;
            Q12=makeQuery(id+"F9.boolean.opBoolean","COPY",FACE,{"derivedFrom":makeQuery(id+"F9.opExtrude","CAP_FACE",FACE,{"disambiguationData":[OSD([sQuery(id+"F8.wireOp",EDGE,"E7.bottom"),sQuery(id+"F8.wireOp",EDGE,"E7.top"),sQuery(id+"F8.wireOp",EDGE,"E7.left"),sQuery(id+"F8.wireOp",EDGE,"E7.right")])],"isStart":false})});
            var Q13;
            Q13=makeQuery(id+"F9.boolean.opBoolean","COPY",FACE,{"derivedFrom":makeQuery(id+"F9.opExtrude","CAP_FACE",FACE,{"disambiguationData":[OSD([sQuery(id+"F8.wireOp",EDGE,"E9.MirrorCS"),sQuery(id+"F8.wireOp",EDGE,"E10.MirrorCS"),sQuery(id+"F8.wireOp",EDGE,"E11.MirrorCS"),sQuery(id+"F8.wireOp",EDGE,"E12.MirrorCS")])],"isStart":false})});
            var Q14;
            {var subQ0=sQuery(id+"F0.wireOp",EDGE,"E3");var subQ1=sQuery(id+"F0.wireOp",EDGE,"E1");var subQ2=makeQuery(id+"F1.opExtrude","CAP_FACE",FACE,{"disambiguationData":[OSD([sQuery(id+"F0.wireOp",EDGE,"E0"),subQ1,sQuery(id+"F0.wireOp",EDGE,"E2"),subQ0])],"isStart":true});var subQ3=makeQuery(id+"F1.opExtrude","CAP_EDGE",EDGE,{"disambiguationData":[OSD([subQ0])],"isStart":true});var subQ5=makeQuery(id+"F9.opExtrude","SWEPT_FACE",FACE,{"disambiguationData":[OSD([sQuery(id+"F8.wireOp",EDGE,"E10.MirrorCS")])]});Q14=makeQuery(id+"F10.boolean.opBoolean","SPLIT",EDGE,{"disambiguationData":[TD([makeQuery(id+"F9.boolean.opBoolean","COPY",FACE,{"derivedFrom":subQ5})])],"derivedFrom":makeQuery(id+"F9.boolean.opBoolean","SPLIT",EDGE,{"disambiguationData":[TD([subQ5])],"derivedFrom":makeQuery(id+"F2.opFillet","BLEND_EDGE",EDGE,{"blendedFrom":[subQ3,subQ2],"blendedInto":[subQ2]})})});}
            var Q15;
            {var subQ0=sQuery(id+"F0.wireOp",EDGE,"E3");var subQ1=sQuery(id+"F0.wireOp",EDGE,"E1");var subQ2=makeQuery(id+"F1.opExtrude","CAP_FACE",FACE,{"disambiguationData":[OSD([sQuery(id+"F0.wireOp",EDGE,"E0"),subQ1,sQuery(id+"F0.wireOp",EDGE,"E2"),subQ0])],"isStart":false});var subQ3=makeQuery(id+"F1.opExtrude","CAP_EDGE",EDGE,{"disambiguationData":[OSD([subQ0])],"isStart":false});var subQ5=makeQuery(id+"F9.opExtrude","SWEPT_FACE",FACE,{"disambiguationData":[OSD([sQuery(id+"F8.wireOp",EDGE,"E7.top")])]});Q15=makeQuery(id+"F10.boolean.opBoolean","SPLIT",EDGE,{"disambiguationData":[TD([makeQuery(id+"F9.boolean.opBoolean","COPY",FACE,{"derivedFrom":subQ5})])],"derivedFrom":makeQuery(id+"F9.boolean.opBoolean","SPLIT",EDGE,{"disambiguationData":[TD([subQ5])],"derivedFrom":makeQuery(id+"F2.opFillet","BLEND_EDGE",EDGE,{"blendedFrom":[subQ3,subQ2],"blendedInto":[subQ2]})})});}
            var Q16;
            Q16=makeQuery(id+"F11.boolean.opBoolean","COPY",EDGE,{"derivedFrom":makeQuery(id+"F11.opExtrude","CAP_EDGE",EDGE,{"disambiguationData":[OSD([sQuery(id+"F8.wireOp",EDGE,"E13.right")])],"isStart":false})});
            var Q17;
            Q17=makeQuery(id+"F11.boolean.opBoolean","COPY",EDGE,{"derivedFrom":makeQuery(id+"F11.opExtrude","CAP_EDGE",EDGE,{"disambiguationData":[OSD([sQuery(id+"F8.wireOp",EDGE,"E15.MirrorCS")])],"isStart":false})});
            var Q18;
            {var subQ0=sQuery(id+"F8.wireOp",EDGE,"E13.bottom");Q18=makeQuery(id+"F11.boolean.opBoolean","MERGE",FACE,{"derivedFrom":[makeQuery(id+"F10.boolean.opBoolean","COPY",FACE,{"derivedFrom":makeQuery(id+"F10.opExtrude","SWEPT_FACE",FACE,{"disambiguationData":[OSD([subQ0])]})})],"fromTools":[makeQuery(id+"F11.opExtrude","SWEPT_FACE",FACE,{"disambiguationData":[OSD([subQ0])]})]});}
            var Q19;
            {var subQ0=sQuery(id+"F8.wireOp",EDGE,"E16.MirrorCS");Q19=makeQuery(id+"F11.boolean.opBoolean","MERGE",FACE,{"derivedFrom":[makeQuery(id+"F10.boolean.opBoolean","COPY",FACE,{"derivedFrom":makeQuery(id+"F10.opExtrude","SWEPT_FACE",FACE,{"disambiguationData":[OSD([subQ0])]})})],"fromTools":[makeQuery(id+"F11.opExtrude","SWEPT_FACE",FACE,{"disambiguationData":[OSD([subQ0])]})]});}
            var Q20;
            Q20=makeQuery(id+"F11.boolean.opBoolean","INTERSECT",EDGE,{"derivedFrom":[makeQuery(id+"F1.opExtrude","CAP_FACE",FACE,{"disambiguationData":[OSD([sQuery(id+"F0.wireOp",EDGE,"E0"),sQuery(id+"F0.wireOp",EDGE,"E1"),sQuery(id+"F0.wireOp",EDGE,"E2"),sQuery(id+"F0.wireOp",EDGE,"E3")])],"isStart":false}),makeQuery(id+"F11.opExtrude","CAP_FACE",FACE,{"disambiguationData":[OSD([sQuery(id+"F8.wireOp",EDGE,"E13.bottom"),sQuery(id+"F8.wireOp",EDGE,"E13.top"),sQuery(id+"F8.wireOp",EDGE,"E13.left"),sQuery(id+"F8.wireOp",EDGE,"E13.right")])],"isStart":false})]});
            var Q21;
            Q21=makeQuery(id+"F11.boolean.opBoolean","INTERSECT",EDGE,{"derivedFrom":[makeQuery(id+"F1.opExtrude","CAP_FACE",FACE,{"disambiguationData":[OSD([sQuery(id+"F0.wireOp",EDGE,"E0"),sQuery(id+"F0.wireOp",EDGE,"E1"),sQuery(id+"F0.wireOp",EDGE,"E2"),sQuery(id+"F0.wireOp",EDGE,"E3")])],"isStart":true}),makeQuery(id+"F11.opExtrude","CAP_FACE",FACE,{"disambiguationData":[OSD([sQuery(id+"F8.wireOp",EDGE,"E14.MirrorCS"),sQuery(id+"F8.wireOp",EDGE,"E15.MirrorCS"),sQuery(id+"F8.wireOp",EDGE,"E16.MirrorCS"),sQuery(id+"F8.wireOp",EDGE,"E17.MirrorCS")])],"isStart":false})]});
            var Q22;
            Q22=makeQuery(id+"F11.boolean.opBoolean","COPY",EDGE,{"derivedFrom":makeQuery(id+"F11.opExtrude","CAP_EDGE",EDGE,{"disambiguationData":[OSD([sQuery(id+"F8.wireOp",EDGE,"E14.MirrorCS")])],"isStart":false})});
            var Q23;
            Q23=makeQuery(id+"F11.boolean.opBoolean","COPY",EDGE,{"derivedFrom":makeQuery(id+"F11.opExtrude","CAP_EDGE",EDGE,{"disambiguationData":[OSD([sQuery(id+"F8.wireOp",EDGE,"E13.top")])],"isStart":false})});
            var Q24;
            {var subQ0=sQuery(id+"F8.wireOp",EDGE,"E13.right");var subQ1=sQuery(id+"F8.wireOp",EDGE,"E13.top");Q24=makeQuery(id+"F11.boolean.opBoolean","MERGE",EDGE,{"derivedFrom":[makeQuery(id+"F10.boolean.opBoolean","COPY",EDGE,{"derivedFrom":makeQuery(id+"F10.opExtrude","SWEPT_EDGE",EDGE,{"disambiguationData":[OSD([subQ1,subQ0])]})})],"fromTools":[makeQuery(id+"F11.opExtrude","SWEPT_EDGE",EDGE,{"disambiguationData":[OSD([subQ1,subQ0])]})]});}
            var Q25;
            {var subQ0=sQuery(id+"F8.wireOp",EDGE,"E15.MirrorCS");var subQ1=sQuery(id+"F8.wireOp",EDGE,"E14.MirrorCS");Q25=makeQuery(id+"F11.boolean.opBoolean","MERGE",EDGE,{"derivedFrom":[makeQuery(id+"F10.boolean.opBoolean","COPY",EDGE,{"derivedFrom":makeQuery(id+"F10.opExtrude","SWEPT_EDGE",EDGE,{"disambiguationData":[OSD([subQ1,subQ0])]})})],"fromTools":[makeQuery(id+"F11.opExtrude","SWEPT_EDGE",EDGE,{"disambiguationData":[OSD([subQ1,subQ0])]})]});}
            fillet(context, id + "F31", {"entities" : qUnion([Q0, Q1, Q2, Q3, Q4, Q5, Q6, Q7, Q8, Q9, Q10, Q11, Q12, Q13, Q14, Q15, Q16, Q17, Q18, Q19, Q20, Q21, Q22, Q23, Q24, Q25]), "radius" : 3 * mm, "tangentPropagation" : true, "allowEdgeOverflow" : false});
        }
        {
            var Q0;
            Q0=makeQuery(id+"F8.imprint","IMPRINT",FACE,{"disambiguationData":[TD([[makeQuery(id+"F8.imprint","IMPRINT",EDGE,{"derivedFrom":sQuery(id+"F8.wireOp",EDGE,"E22")}),1.0]])]});
            var Q1;
            Q1=makeQuery(id+"F8.imprint","IMPRINT",FACE,{"disambiguationData":[TD([[makeQuery(id+"F8.imprint","IMPRINT",EDGE,{"derivedFrom":sQuery(id+"F8.wireOp",EDGE,"E21")}),1.0]])]});
            extrude(context, id + "F32", {"entities" : qUnion([Q0, Q1]), "operationType" : NewBodyOperationType.REMOVE, "depth" : 352 * mm, "offsetDistance" : 25 * mm});
        }
        {
            var Q0;
            Q0=makeQuery(id+"F12.boolean.opBoolean","COPY",FACE,{"derivedFrom":makeQuery(id+"F12.opExtrude","SWEPT_FACE",FACE,{"disambiguationData":[OSD([sQuery(id+"F8.wireOp",EDGE,"E19.top")])]})});
            var sketch = newSketch(context, id + "F33", { "sketchPlane" : qUnion([Q0])});
            skCircle(sketch, "E33", {"center": v(0, 76.08) * mm, "radius": 10 * mm});
            skPoint(sketch, "E33.centerSnap0", {"position": v(75, 76.08) * mm});
            skPoint(sketch, "E33.centerSnap1", {"position": v(0, 10) * mm});
            skSolve(sketch);
        }
        {
            var Q0;
            Q0=makeQuery(id+"F33.imprint","IMPRINT",FACE,{"disambiguationData":[TD([[makeQuery(id+"F33.imprint","IMPRINT",EDGE,{"derivedFrom":sQuery(id+"F33.wireOp",EDGE,"E33")}),1.0]])]});
            extrude(context, id + "F34", {"entities" : qUnion([Q0]), "operationType" : NewBodyOperationType.REMOVE, "oppositeDirection" : true, "depth" : 20 * mm, "offsetDistance" : 25 * mm});
        }
        {
            var Q0;
            Q0=makeQuery(id+"F8.imprint","IMPRINT",FACE,{"disambiguationData":[TD([[makeQuery(id+"F8.imprint","IMPRINT",EDGE,{"derivedFrom":sQuery(id+"F8.wireOp",EDGE,"E24")}),1.0]])]});
            var Q1;
            Q1=makeQuery(id+"F8.imprint","IMPRINT",FACE,{"disambiguationData":[TD([[makeQuery(id+"F8.imprint","IMPRINT",EDGE,{"derivedFrom":sQuery(id+"F8.wireOp",EDGE,"E23")}),1.0]])]});
            extrude(context, id + "F35", {"entities" : qUnion([Q0, Q1]), "operationType" : NewBodyOperationType.REMOVE, "depth" : 330 * mm, "offsetDistance" : 25 * mm});
        }
        {
            var Q0;
            {var subQ0=sQuery(id+"F8.wireOp",EDGE,"E13.right");Q0=makeQuery(id+"F11.boolean.opBoolean","MERGE",FACE,{"derivedFrom":[makeQuery(id+"F10.boolean.opBoolean","COPY",FACE,{"derivedFrom":makeQuery(id+"F10.opExtrude","SWEPT_FACE",FACE,{"disambiguationData":[OSD([subQ0])]})})],"fromTools":[makeQuery(id+"F11.opExtrude","SWEPT_FACE",FACE,{"disambiguationData":[OSD([subQ0])]})]});}
            var sketch = newSketch(context, id + "F36", { "sketchPlane" : qUnion([Q0])});
            skCircle(sketch, "E34", {"center": v(593.25, 111.71) * mm, "radius": 10 * mm});
            skLineSegment(sketch, "E35", {"start": v(593.25, 111.71) * mm, "end": v(533.25, 111.71) * mm});
            skCircle(sketch, "E36", {"center": v(533.25, 111.71) * mm, "radius": 10 * mm});
            skLineSegment(sketch, "E37", {"start": v(533.25, 111.71) * mm, "end": v(-46.75, 111.71) * mm});
            skCircle(sketch, "E38", {"center": v(-46.75, 111.71) * mm, "radius": 10 * mm});
            skSolve(sketch);
        }
        {
            var Q0;
            Q0=makeQuery(id+"F36.imprint","IMPRINT",FACE,{"disambiguationData":[TD([[makeQuery(id+"F36.imprint","IMPRINT",EDGE,{"derivedFrom":sQuery(id+"F36.wireOp",EDGE,"E36")}),1.0]])]});
            var Q1;
            Q1=makeQuery(id+"F36.imprint","IMPRINT",FACE,{"disambiguationData":[TD([[makeQuery(id+"F36.imprint","IMPRINT",EDGE,{"derivedFrom":sQuery(id+"F36.wireOp",EDGE,"E34")}),1.0]])]});
            extrude(context, id + "F37", {"entities" : qUnion([Q0, Q1]), "operationType" : NewBodyOperationType.REMOVE, "oppositeDirection" : true, "depth" : 20 * mm, "offsetDistance" : 25 * mm});
        }
        {
            var Q0;
            {var subQ0=sQuery(id+"F8.wireOp",EDGE,"E15.MirrorCS");Q0=makeQuery(id+"F11.boolean.opBoolean","MERGE",FACE,{"derivedFrom":[makeQuery(id+"F10.boolean.opBoolean","COPY",FACE,{"derivedFrom":makeQuery(id+"F10.opExtrude","SWEPT_FACE",FACE,{"disambiguationData":[OSD([subQ0])]})})],"fromTools":[makeQuery(id+"F11.opExtrude","SWEPT_FACE",FACE,{"disambiguationData":[OSD([subQ0])]})]});}
            var sketch = newSketch(context, id + "F38", { "sketchPlane" : qUnion([Q0])});
            skCircle(sketch, "E39", {"center": v(-585.1, 111.8) * mm, "radius": 10 * mm});
            skLineSegment(sketch, "E40", {"start": v(-585.1, 111.8) * mm, "end": v(-525.1, 111.8) * mm});
            skCircle(sketch, "E41", {"center": v(-525.1, 111.8) * mm, "radius": 10 * mm});
            skLineSegment(sketch, "E42", {"start": v(-525.1, 111.8) * mm, "end": v(54.9, 111.8) * mm});
            skCircle(sketch, "E43", {"center": v(54.9, 111.8) * mm, "radius": 10 * mm});
            skSolve(sketch);
        }
        {
            var Q0;
            Q0=makeQuery(id+"F38.imprint","IMPRINT",FACE,{"disambiguationData":[TD([[makeQuery(id+"F38.imprint","IMPRINT",EDGE,{"derivedFrom":sQuery(id+"F38.wireOp",EDGE,"E39")}),1.0]])]});
            var Q1;
            Q1=makeQuery(id+"F38.imprint","IMPRINT",FACE,{"disambiguationData":[TD([[makeQuery(id+"F38.imprint","IMPRINT",EDGE,{"derivedFrom":sQuery(id+"F38.wireOp",EDGE,"E41")}),1.0]])]});
            extrude(context, id + "F39", {"entities" : qUnion([Q0, Q1]), "operationType" : NewBodyOperationType.REMOVE, "oppositeDirection" : true, "depth" : 20 * mm, "offsetDistance" : 25 * mm});
        }
        {
            var Q0;
            Q0=makeQuery(id+"F25.boolean.opBoolean","COPY",FACE,{"derivedFrom":makeQuery(id+"F25.opExtrude","CAP_FACE",FACE,{"disambiguationData":[OSD([sQuery(id+"F24.wireOp",EDGE,"E29.bottom"),sQuery(id+"F24.wireOp",EDGE,"E29.top"),sQuery(id+"F24.wireOp",EDGE,"E29.left"),sQuery(id+"F24.wireOp",EDGE,"E29.right")])],"isStart":false})});
            var sketch = newSketch(context, id + "F40", { "sketchPlane" : qUnion([Q0])});
            skCircle(sketch, "E44", {"center": v(-75, 22.02) * mm, "radius": 17.5 * mm});
            skSolve(sketch);
        }
        {
            var Q0;
            Q0=makeQuery(id+"F40.imprint","IMPRINT",FACE,{"disambiguationData":[TD([[makeQuery(id+"F40.imprint","IMPRINT",EDGE,{"derivedFrom":sQuery(id+"F40.wireOp",EDGE,"E44")}),1.0]])]});
            var Q1;
            Q1=sQuery(id+"F40.wireOp",EDGE,"E44");
            extrude(context, id + "F41", {"entities" : qUnion([Q0]), "operationType" : NewBodyOperationType.REMOVE, "surfaceEntities" : qUnion([Q1]), "oppositeDirection" : true, "depth" : 20 * mm, "offsetDistance" : 25 * mm});
        }
        {
            var Q0;
            {var subQ1=sQuery(id+"F27.wireOp",EDGE,"E30.bottom");Q0=makeQuery(id+"F28.boolean.opBoolean","COPY",FACE,{"disambiguationData":[TD([makeQuery(id+"F25.boolean.opBoolean","COPY",FACE,{"derivedFrom":makeQuery(id+"F25.opExtrude","SWEPT_FACE",FACE,{"disambiguationData":[OSD([sQuery(id+"F24.wireOp",EDGE,"E29.right")])]})})])],"derivedFrom":makeQuery(id+"F28.opExtrude","SWEPT_FACE",FACE,{"disambiguationData":[OSD([subQ1])]})});}
            var sketch = newSketch(context, id + "F42", { "sketchPlane" : qUnion([Q0])});
            skCircle(sketch, "E45", {"center": v(-150.3, 38.23) * mm, "radius": 15 * mm});
            skLineSegment(sketch, "E46", {"start": v(-150.3, 38.23) * mm, "end": v(149.7, 38.23) * mm});
            skCircle(sketch, "E47", {"center": v(149.7, 38.23) * mm, "radius": 15 * mm});
            skSolve(sketch);
        }
        {
            var Q0;
            Q0=makeQuery(id+"F42.imprint","IMPRINT",FACE,{"disambiguationData":[TD([[makeQuery(id+"F42.imprint","IMPRINT",EDGE,{"derivedFrom":sQuery(id+"F42.wireOp",EDGE,"E45")}),1.0]])]});
            var Q1;
            Q1=makeQuery(id+"F42.imprint","IMPRINT",FACE,{"disambiguationData":[TD([[makeQuery(id+"F42.imprint","IMPRINT",EDGE,{"derivedFrom":sQuery(id+"F42.wireOp",EDGE,"E47")}),1.0]])]});
            extrude(context, id + "F43", {"entities" : qUnion([Q0, Q1]), "operationType" : NewBodyOperationType.REMOVE, "oppositeDirection" : true, "depth" : 20 * mm, "offsetDistance" : 25 * mm});
        }
        {
            var Q0;
            Q0 = qSketchRegion(id + "F38", true);
            var Q1;
            {var subQ0=sQuery(id+"F0.wireOp",EDGE,"E0");var subQ1=sQuery(id+"F0.wireOp",EDGE,"E1");var subQ2=sQuery(id+"F0.wireOp",EDGE,"E3");Q1=makeQuery(id+"F19.boolean.opBoolean","SPLIT",FACE,{"disambiguationData":[TD([makeQuery(id+"F19.opExtrude","SWEPT_FACE",FACE,{"disambiguationData":[OSD([sQuery(id+"F18.wireOp",EDGE,"E27.left")])]})])],"derivedFrom":makeQuery(id+"F1.opExtrude","CAP_FACE",FACE,{"disambiguationData":[OSD([subQ0,subQ1,sQuery(id+"F0.wireOp",EDGE,"E2"),subQ2])],"isStart":true})});}
            extrude(context, id + "F44", {"entities" : qUnion([Q0, Q1]), "operationType" : NewBodyOperationType.REMOVE, "depth" : 150 * mm, "offsetDistance" : 25 * mm});
        }
        {
            var Q0;
            Q0 = qSketchRegion(id + "F36", true);
            extrude(context, id + "F45", {"entities" : qUnion([Q0]), "operationType" : NewBodyOperationType.REMOVE, "depth" : 150 * mm, "offsetDistance" : 25 * mm});
        }
    });
